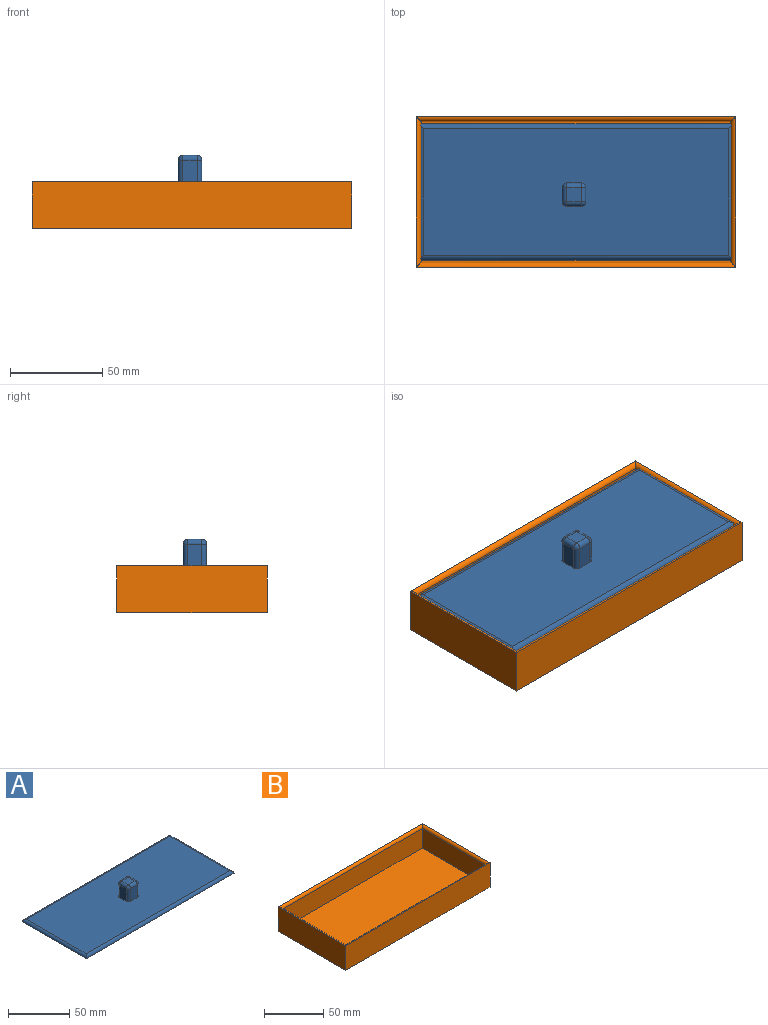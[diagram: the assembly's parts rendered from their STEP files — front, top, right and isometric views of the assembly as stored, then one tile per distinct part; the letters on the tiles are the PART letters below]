
ASSEMBLY  parts=2 mates=1
PART A: 23 faces, bbox 170.2x73.7x17.8 mm
  f0: plane 165.1x68.58mm, normal (0,0,1), area 11166.8mm2, adj f2,f3,f4,f5,f7,f9,f12,f18
  f1: plane 170.18x73.66mm, normal (0,0,-1), area 12535.5mm2, adj f19,f20,f21,f22
  f2: plane 12.7x7.62mm, normal (0,1,0), area 96.8mm2, adj f0,f9,f15,f18
  f3: plane 12.7x7.62mm, normal (-1,0,0), area 96.8mm2, adj f0,f12,f16,f18
  f4: plane 12.7x7.62mm, normal (0,-1,0), area 96.8mm2, adj f0,f7,f11,f12
  f5: plane 12.7x7.62mm, normal (1,0,0), area 96.8mm2, adj f0,f7,f9,f10
  f6: plane 7.62x7.62mm, normal (0,0,1), area 58.1mm2, adj f10,f11,f15,f16
  f7: cylinder r=2.54mm len=12.7mm, axis (0,0,-1), area 50.7mm2, adj f0,f4,f5,f8
  f8: sphere r=2.54mm, area 10.1mm2, adj f7,f10,f11
  f9: cylinder r=2.54mm len=12.7mm, axis (0,0,1), area 50.7mm2, adj f0,f2,f5,f13
  f10: cylinder r=2.54mm len=7.62mm, axis (0,-1,0), area 30.4mm2, adj f5,f6,f8,f13
  f11: cylinder r=2.54mm len=7.62mm, axis (-1,0,0), area 30.4mm2, adj f4,f6,f8,f14
  f12: cylinder r=2.54mm len=12.7mm, axis (0,0,1), area 50.7mm2, adj f0,f3,f4,f14
  f13: sphere r=2.54mm, area 10.1mm2, adj f9,f10,f15
  f14: sphere r=2.54mm, area 10.1mm2, adj f11,f12,f16
  f15: cylinder r=2.54mm len=7.62mm, axis (1,0,0), area 30.4mm2, adj f2,f6,f13,f17
  f16: cylinder r=2.54mm len=7.62mm, axis (0,1,0), area 30.4mm2, adj f3,f6,f14,f17
  f17: sphere r=2.54mm, area 10.1mm2, adj f15,f16,f18
  f18: cylinder r=2.54mm len=12.7mm, axis (0,0,-1), area 50.7mm2, adj f0,f2,f3,f17
  f19: cylinder r=2.54mm len=170.18mm, axis (1,0,0), area 671.6mm2, adj f0,f1,f20,f21
  f20: cylinder r=2.54mm len=73.66mm, axis (0,1,0), area 286.5mm2, adj f0,f1,f19,f22
  f21: cylinder r=2.54mm len=73.66mm, axis (0,-1,0), area 286.5mm2, adj f0,f1,f19,f22
  f22: cylinder r=2.54mm len=170.18mm, axis (-1,0,0), area 671.6mm2, adj f0,f1,f20,f21
PART B: 14 faces, bbox 172.7x81.3x25.4 mm
  f0: plane 172.72x25.4mm, normal (0,1,0), area 4387.1mm2, adj f1,f3,f4,f10
  f1: plane 81.28x25.4mm, normal (-1,0,0), area 2064.5mm2, adj f0,f2,f4,f11
  f2: plane 172.72x25.4mm, normal (0,-1,0), area 4387.1mm2, adj f1,f3,f4,f13
  f3: plane 81.28x25.4mm, normal (1,0,0), area 2064.5mm2, adj f0,f2,f4,f12
  f4: plane 172.72x81.28mm, normal (0,0,-1), area 14038.7mm2, adj f0,f1,f2,f3
  f5: plane 167.64x20.32mm, normal (0,-1,0), area 3406.4mm2, adj f6,f8,f9,f10
  f6: plane 76.2x20.32mm, normal (1,0,0), area 1548.4mm2, adj f5,f7,f9,f11
  f7: plane 167.64x20.32mm, normal (0,1,0), area 3406.4mm2, adj f6,f8,f9,f13
  f8: plane 76.2x20.32mm, normal (-1,0,0), area 1548.4mm2, adj f5,f7,f9,f12
  f9: plane 167.64x76.2mm, normal (0,0,1), area 12774.2mm2, adj f5,f6,f7,f8
  f10: cylinder r=2.54mm len=172.72mm, axis (1,0,0), area 676.2mm2, adj f0,f5,f11,f12
  f11: cylinder r=2.54mm len=81.28mm, axis (0,1,0), area 311.4mm2, adj f1,f6,f10,f13
  f12: cylinder r=2.54mm len=81.28mm, axis (0,-1,0), area 311.4mm2, adj f3,f8,f10,f13
  f13: cylinder r=2.54mm len=172.72mm, axis (-1,0,0), area 676.2mm2, adj f2,f7,f11,f12
PLACE A t=(-9.64,-0.42,21.92)mm
PLACE B t=(-8.56,-0.42,0)mm
MATE slider A.f1 <-> B.f9  axis (0,0,-1) through (-8.56,-0.42,21.92)mm
